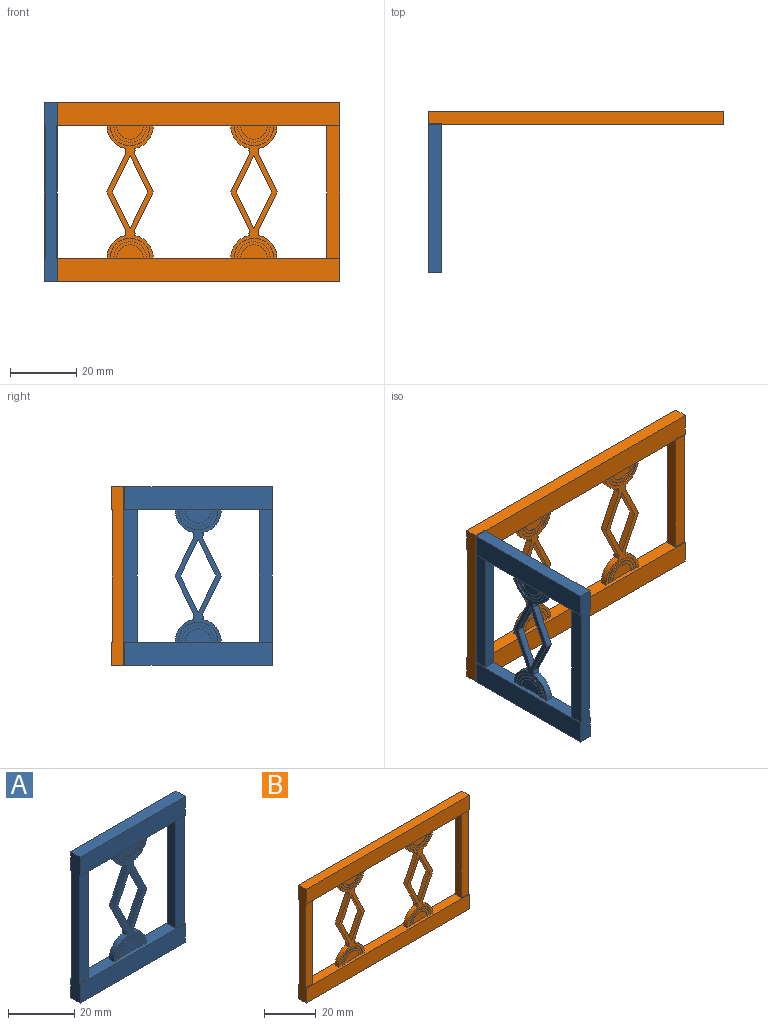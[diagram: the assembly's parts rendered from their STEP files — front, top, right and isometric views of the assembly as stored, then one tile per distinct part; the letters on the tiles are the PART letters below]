
ASSEMBLY  parts=2 mates=1
PART A: 58 faces, bbox 45x4x54 mm
  f0: plane 45x4mm, normal (0,0,1), area 129mm2, adj f2,f3,f4,f5,f6,f7,f8,f13
  f1: plane 45x4mm, normal (0,0,-1), area 129mm2, adj f9,f20,f21,f22,f28,f29,f30,f31
  f2: cylinder r=4mm len=8mm, axis (0,1,0), area 3.1mm2, adj f0,f7,f43
  f3: cylinder r=5mm len=10mm, axis (0,1,0), area 3.9mm2, adj f0,f7,f41
  f4: cylinder r=4mm len=8mm, axis (0,1,0), area 3.1mm2, adj f0,f6,f42
  f5: cylinder r=5mm len=10mm, axis (0,1,0), area 3.9mm2, adj f0,f6,f40
  f6: plane 10x5mm, normal (0,-1,0), area 14.1mm2, adj f0,f4,f5
  f7: plane 10x5mm, normal (0,1,0), area 14.1mm2, adj f0,f2,f3
  f8: cylinder r=6mm len=12mm, axis (0,1,0), area 4.7mm2, adj f0,f29,f41
  f9: cylinder r=6mm len=12mm, axis (0,1,0), area 4.7mm2, adj f1,f29,f37
  f10: plane 11x5.33mm, normal (-0.9,0,0.44), area 24.4mm2, adj f11,f27,f28,f29
  f11: plane 11x5.33mm, normal (0.9,0,0.44), area 24.4mm2, adj f10,f12,f28,f29
  f12: plane 11x5.33mm, normal (0.9,0,-0.44), area 24.4mm2, adj f11,f27,f28,f29
  f13: cylinder r=7mm len=6.87mm, axis (0,1,0), area 19.3mm2, adj f0,f26,f28,f29
  f14: cylinder r=6mm len=12mm, axis (0,1,0), area 4.7mm2, adj f0,f28,f40
  f15: cylinder r=7mm len=6.87mm, axis (0,1,0), area 19.3mm2, adj f0,f16,f28,f29
  f16: cylinder r=1.5mm len=2mm, axis (0,1,0), area 2.9mm2, adj f15,f17,f28,f29
  f17: plane 11.75x5.7mm, normal (0.9,0,-0.44), area 26.1mm2, adj f16,f18,f28,f29
  f18: plane 11.75x5.7mm, normal (0.9,0,0.44), area 26.1mm2, adj f17,f19,f28,f29
  f19: cylinder r=1.5mm len=2mm, axis (0,1,0), area 2.9mm2, adj f18,f20,f28,f29
  f20: cylinder r=7mm len=6.87mm, axis (0,1,0), area 19.3mm2, adj f1,f19,f28,f29
  f21: cylinder r=6mm len=12mm, axis (0,1,0), area 4.7mm2, adj f1,f28,f36
  f22: cylinder r=7mm len=6.87mm, axis (0,1,0), area 19.3mm2, adj f1,f23,f28,f29
  f23: cylinder r=1.5mm len=2mm, axis (0,1,0), area 2.9mm2, adj f22,f24,f28,f29
  f24: plane 11.75x5.7mm, normal (-0.9,0,0.44), area 26.1mm2, adj f23,f25,f28,f29
  f25: plane 11.75x5.7mm, normal (-0.9,0,-0.44), area 26.1mm2, adj f24,f26,f28,f29
  f26: cylinder r=1.5mm len=2mm, axis (0,1,0), area 2.9mm2, adj f13,f25,f28,f29
  f27: plane 11x5.33mm, normal (-0.9,0,-0.44), area 24.4mm2, adj f10,f12,f28,f29
  f28: plane 40x14mm, normal (0,-1,0), area 126.1mm2, adj f0,f1,f10,f11,f12,f13,f14,f15
  f29: plane 40x14mm, normal (0,1,0), area 126.1mm2, adj f0,f1,f8,f9,f10,f11,f12,f13
  f30: cylinder r=4mm len=8mm, axis (0,1,0), area 3.1mm2, adj f1,f35,f39
  f31: cylinder r=5mm len=10mm, axis (0,1,0), area 3.9mm2, adj f1,f35,f37
  f32: cylinder r=4mm len=8mm, axis (0,1,0), area 3.1mm2, adj f1,f34,f38
  f33: cylinder r=5mm len=10mm, axis (0,1,0), area 3.9mm2, adj f1,f34,f36
  f34: plane 10x5mm, normal (0,-1,0), area 14.1mm2, adj f1,f32,f33
  f35: plane 10x5mm, normal (0,1,0), area 14.1mm2, adj f1,f30,f31
  f36: plane 12x6mm, normal (0,-1,0), area 17.3mm2, adj f1,f21,f33
  f37: plane 12x6mm, normal (0,1,0), area 17.3mm2, adj f1,f9,f31
  f38: plane 8x4mm, normal (0,-1,0), area 25.1mm2, adj f1,f32
  f39: plane 8x4mm, normal (0,1,0), area 25.1mm2, adj f1,f30
  f40: plane 12x6mm, normal (0,-1,0), area 17.3mm2, adj f0,f5,f14
  f41: plane 12x6mm, normal (0,1,0), area 17.3mm2, adj f0,f3,f8
  f42: plane 8x4mm, normal (0,-1,0), area 25.1mm2, adj f0,f4
  f43: plane 8x4mm, normal (0,1,0), area 25.1mm2, adj f0,f2
  f44: plane 54x4mm, normal (-1,0,0), area 196mm2, adj f0,f1,f45,f47,f48,f49,f50,f51
  f45: plane 45x4mm, normal (0,0,-1), area 180mm2, adj f44,f46,f47,f48
  f46: plane 54x4mm, normal (1,0,0), area 196mm2, adj f0,f1,f45,f47,f48,f49,f50,f51
  f47: plane 45x7mm, normal (0,-1,0), area 315mm2, adj f0,f44,f45,f46
  f48: plane 45x7mm, normal (0,1,0), area 315mm2, adj f0,f44,f45,f46
  f49: plane 45x4mm, normal (0,0,1), area 180mm2, adj f44,f46,f50,f51
  f50: plane 45x7mm, normal (0,-1,0), area 315mm2, adj f1,f44,f46,f49
  f51: plane 45x7mm, normal (0,1,0), area 315mm2, adj f1,f44,f46,f49
  f52: plane 40x3.5mm, normal (1,0,0), area 140mm2, adj f0,f1,f53,f54
  f53: plane 40x4mm, normal (0,-1,0), area 160mm2, adj f0,f1,f44,f52
  f54: plane 40x4mm, normal (0,1,0), area 160mm2, adj f0,f1,f44,f52
  f55: plane 40x3.5mm, normal (-1,0,0), area 140mm2, adj f0,f1,f56,f57
  f56: plane 40x4mm, normal (0,-1,0), area 160mm2, adj f0,f1,f46,f55
  f57: plane 40x4mm, normal (0,1,0), area 160mm2, adj f0,f1,f46,f55
PART B: 100 faces, bbox 89.5x4x54 mm
  f0: plane 89.5x4mm, normal (0,0,-1), area 284mm2, adj f9,f20,f21,f22,f28,f29,f30,f31
  f1: plane 89.5x4mm, normal (0,0,1), area 284mm2, adj f2,f3,f4,f5,f6,f7,f8,f13
  f2: cylinder r=4mm len=8mm, axis (0,1,0), area 3.1mm2, adj f1,f7,f43
  f3: cylinder r=5mm len=10mm, axis (0,1,0), area 3.9mm2, adj f1,f7,f41
  f4: cylinder r=4mm len=8mm, axis (0,1,0), area 3.1mm2, adj f1,f6,f42
  f5: cylinder r=5mm len=10mm, axis (0,1,0), area 3.9mm2, adj f1,f6,f40
  f6: plane 10x5mm, normal (0,-1,0), area 14.1mm2, adj f1,f4,f5
  f7: plane 10x5mm, normal (0,1,0), area 14.1mm2, adj f1,f2,f3
  f8: cylinder r=6mm len=12mm, axis (0,1,0), area 4.7mm2, adj f1,f29,f41
  f9: cylinder r=6mm len=12mm, axis (0,1,0), area 4.7mm2, adj f0,f29,f37
  f10: plane 11x5.33mm, normal (-0.9,0,0.44), area 24.4mm2, adj f11,f27,f28,f29
  f11: plane 11x5.33mm, normal (0.9,0,0.44), area 24.4mm2, adj f10,f12,f28,f29
  f12: plane 11x5.33mm, normal (0.9,0,-0.44), area 24.4mm2, adj f11,f27,f28,f29
  f13: cylinder r=7mm len=6.87mm, axis (0,1,0), area 19.3mm2, adj f1,f26,f28,f29
  f14: cylinder r=6mm len=12mm, axis (0,1,0), area 4.7mm2, adj f1,f28,f40
  f15: cylinder r=7mm len=6.87mm, axis (0,1,0), area 19.3mm2, adj f1,f16,f28,f29
  f16: cylinder r=1.5mm len=2mm, axis (0,1,0), area 2.9mm2, adj f15,f17,f28,f29
  f17: plane 11.75x5.7mm, normal (0.9,0,-0.44), area 26.1mm2, adj f16,f18,f28,f29
  f18: plane 11.75x5.7mm, normal (0.9,0,0.44), area 26.1mm2, adj f17,f19,f28,f29
  f19: cylinder r=1.5mm len=2mm, axis (0,1,0), area 2.9mm2, adj f18,f20,f28,f29
  f20: cylinder r=7mm len=6.87mm, axis (0,1,0), area 19.3mm2, adj f0,f19,f28,f29
  f21: cylinder r=6mm len=12mm, axis (0,1,0), area 4.7mm2, adj f0,f28,f36
  f22: cylinder r=7mm len=6.87mm, axis (0,1,0), area 19.3mm2, adj f0,f23,f28,f29
  f23: cylinder r=1.5mm len=2mm, axis (0,1,0), area 2.9mm2, adj f22,f24,f28,f29
  f24: plane 11.75x5.7mm, normal (-0.9,0,0.44), area 26.1mm2, adj f23,f25,f28,f29
  f25: plane 11.75x5.7mm, normal (-0.9,0,-0.44), area 26.1mm2, adj f24,f26,f28,f29
  f26: cylinder r=1.5mm len=2mm, axis (0,1,0), area 2.9mm2, adj f13,f25,f28,f29
  f27: plane 11x5.33mm, normal (-0.9,0,-0.44), area 24.4mm2, adj f10,f12,f28,f29
  f28: plane 40x14mm, normal (0,-1,0), area 126.1mm2, adj f0,f1,f10,f11,f12,f13,f14,f15
  f29: plane 40x14mm, normal (0,1,0), area 126.1mm2, adj f0,f1,f8,f9,f10,f11,f12,f13
  f30: cylinder r=4mm len=8mm, axis (0,1,0), area 3.1mm2, adj f0,f35,f39
  f31: cylinder r=5mm len=10mm, axis (0,1,0), area 3.9mm2, adj f0,f35,f37
  f32: cylinder r=4mm len=8mm, axis (0,1,0), area 3.1mm2, adj f0,f34,f38
  f33: cylinder r=5mm len=10mm, axis (0,1,0), area 3.9mm2, adj f0,f34,f36
  f34: plane 10x5mm, normal (0,-1,0), area 14.1mm2, adj f0,f32,f33
  f35: plane 10x5mm, normal (0,1,0), area 14.1mm2, adj f0,f30,f31
  f36: plane 12x6mm, normal (0,-1,0), area 17.3mm2, adj f0,f21,f33
  f37: plane 12x6mm, normal (0,1,0), area 17.3mm2, adj f0,f9,f31
  f38: plane 8x4mm, normal (0,-1,0), area 25.1mm2, adj f0,f32
  f39: plane 8x4mm, normal (0,1,0), area 25.1mm2, adj f0,f30
  f40: plane 12x6mm, normal (0,-1,0), area 17.3mm2, adj f1,f5,f14
  f41: plane 12x6mm, normal (0,1,0), area 17.3mm2, adj f1,f3,f8
  f42: plane 8x4mm, normal (0,-1,0), area 25.1mm2, adj f1,f4
  f43: plane 8x4mm, normal (0,1,0), area 25.1mm2, adj f1,f2
  f44: cylinder r=4mm len=8mm, axis (0,1,0), area 3.1mm2, adj f1,f49,f85
  f45: cylinder r=5mm len=10mm, axis (0,1,0), area 3.9mm2, adj f1,f49,f83
  f46: cylinder r=4mm len=8mm, axis (0,1,0), area 3.1mm2, adj f1,f48,f84
  f47: cylinder r=5mm len=10mm, axis (0,1,0), area 3.9mm2, adj f1,f48,f82
  f48: plane 10x5mm, normal (0,-1,0), area 14.1mm2, adj f1,f46,f47
  f49: plane 10x5mm, normal (0,1,0), area 14.1mm2, adj f1,f44,f45
  f50: cylinder r=6mm len=12mm, axis (0,1,0), area 4.7mm2, adj f1,f71,f83
  f51: cylinder r=6mm len=12mm, axis (0,1,0), area 4.7mm2, adj f0,f71,f79
  f52: plane 11x5.33mm, normal (-0.9,0,0.44), area 24.4mm2, adj f53,f69,f70,f71
  f53: plane 11x5.33mm, normal (0.9,0,0.44), area 24.4mm2, adj f52,f54,f70,f71
  f54: plane 11x5.33mm, normal (0.9,0,-0.44), area 24.4mm2, adj f53,f69,f70,f71
  f55: cylinder r=7mm len=6.87mm, axis (0,1,0), area 19.3mm2, adj f1,f68,f70,f71
  f56: cylinder r=6mm len=12mm, axis (0,1,0), area 4.7mm2, adj f1,f70,f82
  f57: cylinder r=7mm len=6.87mm, axis (0,1,0), area 19.3mm2, adj f1,f58,f70,f71
  f58: cylinder r=1.5mm len=2mm, axis (0,1,0), area 2.9mm2, adj f57,f59,f70,f71
  f59: plane 11.75x5.7mm, normal (0.9,0,-0.44), area 26.1mm2, adj f58,f60,f70,f71
  f60: plane 11.75x5.7mm, normal (0.9,0,0.44), area 26.1mm2, adj f59,f61,f70,f71
  f61: cylinder r=1.5mm len=2mm, axis (0,1,0), area 2.9mm2, adj f60,f62,f70,f71
  f62: cylinder r=7mm len=6.87mm, axis (0,1,0), area 19.3mm2, adj f0,f61,f70,f71
  f63: cylinder r=6mm len=12mm, axis (0,1,0), area 4.7mm2, adj f0,f70,f78
  f64: cylinder r=7mm len=6.87mm, axis (0,1,0), area 19.3mm2, adj f0,f65,f70,f71
  f65: cylinder r=1.5mm len=2mm, axis (0,1,0), area 2.9mm2, adj f64,f66,f70,f71
  f66: plane 11.75x5.7mm, normal (-0.9,0,0.44), area 26.1mm2, adj f65,f67,f70,f71
  f67: plane 11.75x5.7mm, normal (-0.9,0,-0.44), area 26.1mm2, adj f66,f68,f70,f71
  f68: cylinder r=1.5mm len=2mm, axis (0,1,0), area 2.9mm2, adj f55,f67,f70,f71
  f69: plane 11x5.33mm, normal (-0.9,0,-0.44), area 24.4mm2, adj f52,f54,f70,f71
  f70: plane 40x14mm, normal (0,-1,0), area 126.1mm2, adj f0,f1,f52,f53,f54,f55,f56,f57
  f71: plane 40x14mm, normal (0,1,0), area 126.1mm2, adj f0,f1,f50,f51,f52,f53,f54,f55
  f72: cylinder r=4mm len=8mm, axis (0,1,0), area 3.1mm2, adj f0,f77,f81
  f73: cylinder r=5mm len=10mm, axis (0,1,0), area 3.9mm2, adj f0,f77,f79
  f74: cylinder r=4mm len=8mm, axis (0,1,0), area 3.1mm2, adj f0,f76,f80
  f75: cylinder r=5mm len=10mm, axis (0,1,0), area 3.9mm2, adj f0,f76,f78
  f76: plane 10x5mm, normal (0,-1,0), area 14.1mm2, adj f0,f74,f75
  f77: plane 10x5mm, normal (0,1,0), area 14.1mm2, adj f0,f72,f73
  f78: plane 12x6mm, normal (0,-1,0), area 17.3mm2, adj f0,f63,f75
  f79: plane 12x6mm, normal (0,1,0), area 17.3mm2, adj f0,f51,f73
  f80: plane 8x4mm, normal (0,-1,0), area 25.1mm2, adj f0,f74
  f81: plane 8x4mm, normal (0,1,0), area 25.1mm2, adj f0,f72
  f82: plane 12x6mm, normal (0,-1,0), area 17.3mm2, adj f1,f47,f56
  f83: plane 12x6mm, normal (0,1,0), area 17.3mm2, adj f1,f45,f50
  f84: plane 8x4mm, normal (0,-1,0), area 25.1mm2, adj f1,f46
  f85: plane 8x4mm, normal (0,1,0), area 25.1mm2, adj f1,f44
  f86: plane 54x4mm, normal (-1,0,0), area 196mm2, adj f0,f1,f87,f89,f90,f91,f92,f93
  f87: plane 89.5x4mm, normal (0,0,-1), area 358mm2, adj f86,f88,f89,f90
  f88: plane 54x4mm, normal (1,0,0), area 196mm2, adj f0,f1,f87,f89,f90,f91,f92,f93
  f89: plane 89.5x7mm, normal (0,-1,0), area 626.5mm2, adj f1,f86,f87,f88
  f90: plane 89.5x7mm, normal (0,1,0), area 626.5mm2, adj f1,f86,f87,f88
  f91: plane 89.5x4mm, normal (0,0,1), area 358mm2, adj f86,f88,f92,f93
  f92: plane 89.5x7mm, normal (0,-1,0), area 626.5mm2, adj f0,f86,f88,f91
  f93: plane 89.5x7mm, normal (0,1,0), area 626.5mm2, adj f0,f86,f88,f91
  f94: plane 40x3.5mm, normal (-1,0,0), area 140mm2, adj f0,f1,f95,f96
  f95: plane 40x4mm, normal (0,-1,0), area 160mm2, adj f0,f1,f88,f94
  f96: plane 40x4mm, normal (0,1,0), area 160mm2, adj f0,f1,f88,f94
  f97: plane 40x3.5mm, normal (1,0,0), area 140mm2, adj f0,f1,f98,f99
  f98: plane 40x4mm, normal (0,-1,0), area 160mm2, adj f0,f1,f86,f97
  f99: plane 40x4mm, normal (0,1,0), area 160mm2, adj f0,f1,f86,f97
PLACE A rot(axis=(0,0,-1),90deg) t=(-87.5,-19.25,7)mm
PLACE B rot(axis=(1,0,0),180deg) t=(-70.5,-2,47)mm
MATE fastened A.f44 <-> B.f99  axis (0,1,0) through (-87.5,-3.75,27)mm
